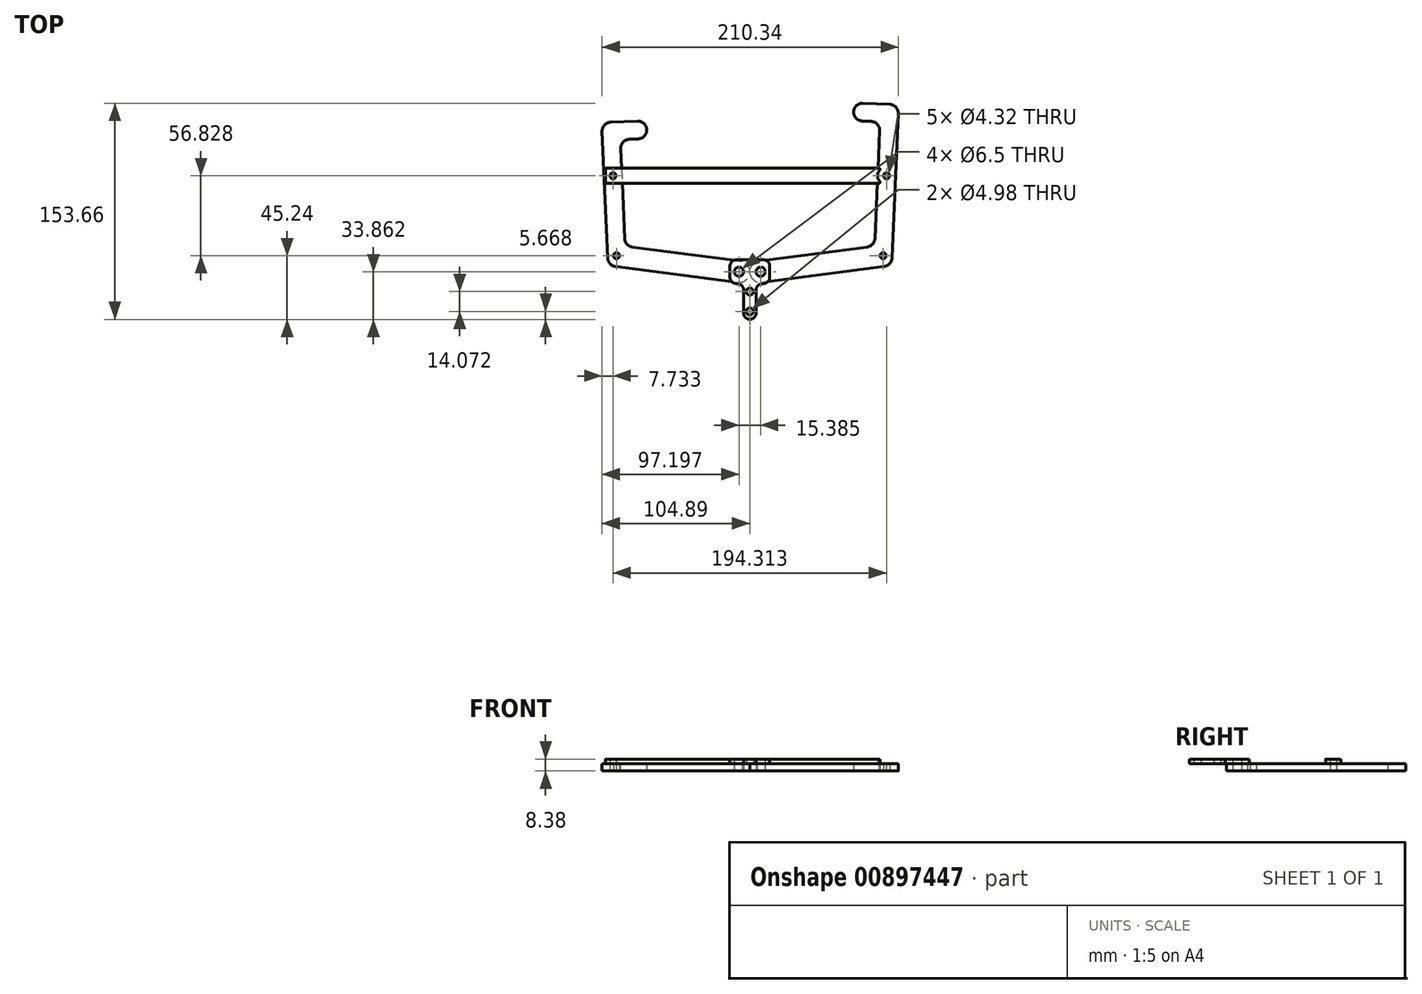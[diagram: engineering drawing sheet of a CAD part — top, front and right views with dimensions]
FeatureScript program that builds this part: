
annotation { "Feature Type Name" : "Feature", "Feature Type Description" : "" }
export const myFeature = defineFeature(function(context is Context, id is Id, definition is map)
    precondition{}
    {
        {
            var Q0;
            Q0=qCreatedBy(makeId("Top.planeOp"),FACE);
            var sketch = newSketch(context, id + "F0", { "sketchPlane" : qUnion([Q0])});
            skLineSegment(sketch, "E0", {"start": v(-105.16, 38.56) * mm, "end": v(-73.44, 39.95) * mm});
            skLineSegment(sketch, "E1", {"start": v(-105.16, 38.56) * mm, "end": v(-100.73, -62.94) * mm});
            skLineSegment(sketch, "E2", {"start": v(-100.73, -62.94) * mm, "end": v(-8.7, -75.06) * mm});
            skCircle(sketch, "E3", {"center": v(-94.68, -56.05) * mm, "radius": 2.16 * mm});
            skCircle(sketch, "E4.MirrorC", {"center": v(94.68, -56.05) * mm, "radius": 2.16 * mm});
            skLineSegment(sketch, "E5", {"start": v(-73.44, 39.95) * mm, "end": v(-72.89, 27.26) * mm});
            skLineSegment(sketch, "E6", {"start": v(-72.89, 27.26) * mm, "end": v(-91.92, 26.43) * mm});
            skLineSegment(sketch, "E7", {"start": v(-91.92, 26.43) * mm, "end": v(-88.62, -49.16) * mm});
            skLineSegment(sketch, "E8", {"start": v(-88.62, -49.16) * mm, "end": v(-5.23, -60.14) * mm});
            skLineSegment(sketch, "E9.MirrorCS", {"start": v(92.47, 39.12) * mm, "end": v(88.62, -49.16) * mm});
            skLineSegment(sketch, "E10.MirrorCS", {"start": v(105.72, 51.25) * mm, "end": v(74, 52.64) * mm});
            skLineSegment(sketch, "E11.MirrorCS", {"start": v(74, 52.64) * mm, "end": v(73.44, 39.95) * mm});
            skLineSegment(sketch, "E12.MirrorCS", {"start": v(100.73, -62.94) * mm, "end": v(8.7, -75.06) * mm});
            skLineSegment(sketch, "E13.MirrorCS", {"start": v(105.72, 51.25) * mm, "end": v(100.73, -62.94) * mm});
            skLineSegment(sketch, "E14.MirrorCS", {"start": v(88.62, -49.16) * mm, "end": v(5.23, -60.14) * mm});
            skLineSegment(sketch, "E15.MirrorCS", {"start": v(73.44, 39.95) * mm, "end": v(92.47, 39.12) * mm});
            skArc(sketch, "E16", {"start": v(-8.7, -75.06) * mm, "mid": v(-0.2, -69.17) * mm, "end": v(-5.23, -60.14) * mm});
            skArc(sketch, "E17.MirrorCS", {"start": v(8.7, -75.06) * mm, "mid": v(0.2, -69.17) * mm, "end": v(5.23, -60.14) * mm});
            skPoint(sketch, "E18.orphan", {"position": v(0, -60.83) * mm});
            skPoint(sketch, "E19.orphan", {"position": v(0, -76.2) * mm});
            skLineSegment(sketch, "E20", {"start": v(-100.73, -62.94) * mm, "end": v(0, -76.2) * mm, "construction": true});
            skPoint(sketch, "E21.middle", {"position": v(0, -67.43) * mm});
            skCircle(sketch, "E22", {"center": v(-7.7, -67.43) * mm, "radius": 3.25 * mm});
            skCircle(sketch, "E23", {"center": v(7.7, -67.43) * mm, "radius": 3.25 * mm});
            skLineSegment(sketch, "E24", {"start": v(-88.62, -49.16) * mm, "end": v(-100.73, -62.94) * mm, "construction": true});
            skCircle(sketch, "E25", {"center": v(-97.16, 0.78) * mm, "radius": 2.16 * mm});
            skCircle(sketch, "E26.MirrorC", {"center": v(97.16, 0.78) * mm, "radius": 2.16 * mm});
            skLineSegment(sketch, "E27", {"start": v(-103.5, 0.5) * mm, "end": v(-90.81, 1.05) * mm, "construction": true});
            skLineSegment(sketch, "E28", {"start": v(0, -76.2) * mm, "end": v(-48.84, -76.2) * mm, "construction": true});
            skSolve(sketch);
        }
        {
            var Q0;
            Q0 = qSketchRegion(id + "F0", true);
            extrude(context, id + "F1", {"entities" : qUnion([Q0]), "depth" : 5.2 * mm, "offsetDistance" : 25.4 * mm});
        }
        {
            var Q0;
            Q0=makeQuery(id+"F1.opExtrude","CAP_FACE",FACE,{"disambiguationData":[OSD([sQuery(id+"F0.wireOp",EDGE,"E0"),sQuery(id+"F0.wireOp",EDGE,"E1"),sQuery(id+"F0.wireOp",EDGE,"E2"),sQuery(id+"F0.wireOp",EDGE,"E3"),sQuery(id+"F0.wireOp",EDGE,"E5"),sQuery(id+"F0.wireOp",EDGE,"E6"),sQuery(id+"F0.wireOp",EDGE,"E7"),sQuery(id+"F0.wireOp",EDGE,"E8"),sQuery(id+"F0.wireOp",EDGE,"E16"),sQuery(id+"F0.wireOp",EDGE,"E22"),sQuery(id+"F0.wireOp",EDGE,"E25")])],"isStart":false});
            var sketch = newSketch(context, id + "F2", { "sketchPlane" : qUnion([Q0])});
            skLineSegment(sketch, "E29.bottom", {"start": v(-4.44, -75.89) * mm, "end": v(4.45, -75.89) * mm});
            skLineSegment(sketch, "E29.top", {"start": v(-4.44, -101.29) * mm, "end": v(4.45, -101.29) * mm});
            skLineSegment(sketch, "E29.left", {"start": v(-4.44, -75.89) * mm, "end": v(-4.44, -101.29) * mm});
            skLineSegment(sketch, "E29.right", {"start": v(4.45, -75.89) * mm, "end": v(4.45, -101.29) * mm});
            skPoint(sketch, "E29.middle", {"position": v(0, -88.59) * mm});
            skCircle(sketch, "E30.0", {"center": v(-7.7, -67.43) * mm, "radius": 3.25 * mm});
            skCircle(sketch, "E30.1", {"center": v(7.7, -67.43) * mm, "radius": 3.25 * mm});
            skCircle(sketch, "E31.cCircle", {"center": v(-121.49, -83.42) * mm, "radius": 6.35 * mm, "construction": true});
            skLineSegment(sketch, "E31.0", {"start": v(-125.16, -77.07) * mm, "end": v(-117.82, -77.07) * mm});
            skLineSegment(sketch, "E31.1", {"start": v(-117.82, -77.07) * mm, "end": v(-114.16, -83.42) * mm});
            skLineSegment(sketch, "E31.2", {"start": v(-114.16, -83.42) * mm, "end": v(-117.82, -89.77) * mm});
            skLineSegment(sketch, "E31.3", {"start": v(-117.82, -89.77) * mm, "end": v(-125.16, -89.77) * mm});
            skLineSegment(sketch, "E31.4", {"start": v(-125.16, -89.77) * mm, "end": v(-128.82, -83.42) * mm});
            skLineSegment(sketch, "E31.5", {"start": v(-128.82, -83.42) * mm, "end": v(-125.16, -77.07) * mm});
            skPoint(sketch, "E31.0.midPoint", {"position": v(-121.49, -77.07) * mm});
            skLineSegment(sketch, "E32.bottom", {"start": v(-14.12, -58.97) * mm, "end": v(14.12, -58.97) * mm});
            skLineSegment(sketch, "E32.top", {"start": v(-14.12, -75.89) * mm, "end": v(14.12, -75.89) * mm});
            skLineSegment(sketch, "E32.left", {"start": v(-14.12, -58.97) * mm, "end": v(-14.12, -75.89) * mm});
            skLineSegment(sketch, "E32.right", {"start": v(14.12, -58.97) * mm, "end": v(14.12, -75.89) * mm});
            skPoint(sketch, "E32.middle", {"position": v(0, -67.43) * mm});
            skCircle(sketch, "E33", {"center": v(0, -81.55) * mm, "radius": 2.49 * mm});
            skLineSegment(sketch, "E34", {"start": v(0, -88.59) * mm, "end": v(-4.44, -88.59) * mm, "construction": true});
            skCircle(sketch, "E35.MirrorC", {"center": v(0, -95.62) * mm, "radius": 2.49 * mm});
            skSolve(sketch);
        }
        {
            var Q0;
            {var subQ1=sQuery(id+"F2.wireOp",EDGE,"E29.bottom");Q0=makeQuery(id+"F2.imprint","IMPRINT",FACE,{"disambiguationData":[TD([[makeQuery(id+"F2.imprint","IMPRINT",EDGE,{"derivedFrom":subQ1}),1.0]])]});}
            var Q1;
            Q1=makeQuery(id+"F2.imprint","IMPRINT",FACE,{"disambiguationData":[TD([[makeQuery(id+"F2.imprint","IMPRINT",EDGE,{"derivedFrom":sQuery(id+"F2.wireOp",EDGE,"E29.bottom")}),-1.0]])]});
            var Q2;
            Q2=makeQuery(id+"F2.imprint","IMPRINT",FACE,{"disambiguationData":[TD([[makeQuery(id+"F2.imprint","IMPRINT",EDGE,{"derivedFrom":sQuery(id+"F2.wireOp",EDGE,"E30.0")}),-1.0]])]});
            extrude(context, id + "F3", {"entities" : qUnion([Q0, Q1, Q2]), "depth" : 3.17 * mm, "offsetDistance" : 25.4 * mm});
        }
        {
            var Q0;
            Q0=makeQuery(id+"F3.opExtrude","SWEPT_EDGE",EDGE,{"disambiguationData":[OSD([sQuery(id+"F2.wireOp",EDGE,"E29.bottom"),sQuery(id+"F2.wireOp",EDGE,"E29.left"),sQuery(id+"F2.wireOp",EDGE,"E32.top")])]});
            var Q1;
            Q1=makeQuery(id+"F3.opExtrude","SWEPT_EDGE",EDGE,{"disambiguationData":[OSD([sQuery(id+"F2.wireOp",EDGE,"E32.top"),sQuery(id+"F2.wireOp",EDGE,"E32.left")])]});
            var Q2;
            Q2=makeQuery(id+"F3.opExtrude","SWEPT_EDGE",EDGE,{"disambiguationData":[OSD([sQuery(id+"F2.wireOp",EDGE,"E29.bottom"),sQuery(id+"F2.wireOp",EDGE,"E29.right"),sQuery(id+"F2.wireOp",EDGE,"E32.top")])]});
            var Q3;
            Q3=makeQuery(id+"F3.opExtrude","SWEPT_EDGE",EDGE,{"disambiguationData":[OSD([sQuery(id+"F2.wireOp",EDGE,"E32.top"),sQuery(id+"F2.wireOp",EDGE,"E32.right")])]});
            var Q4;
            Q4=makeQuery(id+"F3.opExtrude","SWEPT_EDGE",EDGE,{"disambiguationData":[OSD([sQuery(id+"F2.wireOp",EDGE,"E32.bottom"),sQuery(id+"F2.wireOp",EDGE,"E32.right")])]});
            var Q5;
            Q5=makeQuery(id+"F3.opExtrude","SWEPT_EDGE",EDGE,{"disambiguationData":[OSD([sQuery(id+"F0.wireOp",EDGE,"E8"),sQuery(id+"F2.wireOp",EDGE,"E32.bottom"),sQuery(id+"F2.wireOp",EDGE,"E32.left")])]});
            var Q6;
            Q6=makeQuery(id+"F3.opExtrude","SWEPT_EDGE",EDGE,{"disambiguationData":[OSD([sQuery(id+"F2.wireOp",EDGE,"E29.top"),sQuery(id+"F2.wireOp",EDGE,"E29.left")])]});
            var Q7;
            Q7=makeQuery(id+"F3.opExtrude","SWEPT_EDGE",EDGE,{"disambiguationData":[OSD([sQuery(id+"F2.wireOp",EDGE,"E29.top"),sQuery(id+"F2.wireOp",EDGE,"E29.right")])]});
            fillet(context, id + "F4", {"entities" : qUnion([Q0, Q1, Q2, Q3, Q4, Q5, Q6, Q7]), "radius" : 4.44 * mm, "tangentPropagation" : true, "allowEdgeOverflow" : false});
        }
        {
            var Q0;
            Q0=makeQuery(id+"F1.opExtrude","CAP_FACE",FACE,{"disambiguationData":[OSD([sQuery(id+"F0.wireOp",EDGE,"E9.MirrorCS"),sQuery(id+"F0.wireOp",EDGE,"E10.MirrorCS"),sQuery(id+"F0.wireOp",EDGE,"E11.MirrorCS"),sQuery(id+"F0.wireOp",EDGE,"E12.MirrorCS"),sQuery(id+"F0.wireOp",EDGE,"E13.MirrorCS"),sQuery(id+"F0.wireOp",EDGE,"E14.MirrorCS"),sQuery(id+"F0.wireOp",EDGE,"E15.MirrorCS"),sQuery(id+"F0.wireOp",EDGE,"E4.MirrorC"),sQuery(id+"F0.wireOp",EDGE,"E17.MirrorCS"),sQuery(id+"F0.wireOp",EDGE,"E23"),sQuery(id+"F0.wireOp",EDGE,"E26.MirrorC")])],"isStart":false});
            var sketch = newSketch(context, id + "F5", { "sketchPlane" : qUnion([Q0])});
            skCircle(sketch, "E36", {"center": v(97.16, 0.78) * mm, "radius": 6.35 * mm});
            skLineSegment(sketch, "E37.bottom", {"start": v(-102.5, 6.11) * mm, "end": v(93.71, 6.11) * mm});
            skLineSegment(sketch, "E37.top", {"start": v(-102.5, -4.56) * mm, "end": v(93.71, -4.56) * mm});
            skLineSegment(sketch, "E37.left", {"start": v(-102.5, 6.11) * mm, "end": v(-102.5, -4.56) * mm});
            skLineSegment(sketch, "E37.right", {"start": v(93.71, 0.78) * mm, "end": v(93.71, -4.56) * mm});
            skPoint(sketch, "E38", {"position": v(93.71, 0.78) * mm});
            skCircle(sketch, "E39.0", {"center": v(-97.16, 0.78) * mm, "radius": 2.16 * mm});
            skSolve(sketch);
        }
        {
            var Q0;
            {var subQ0=sQuery(id+"F5.wireOp",EDGE,"E37.left");Q0=makeQuery(id+"F5.imprint","IMPRINT",FACE,{"disambiguationData":[TD([[makeQuery(id+"F5.imprint","IMPRINT",EDGE,{"derivedFrom":subQ0}),1.0]])]});}
            var Q1;
            {var subQ0=sQuery(id+"F5.wireOp",EDGE,"E37.top");var subQ1=sQuery(id+"F5.wireOp",EDGE,"E36");var subQ2=makeQuery(id+"F5.imprint","INTERSECT",VERTEX,{"derivedFrom":[subQ1,subQ0]});Q1=makeQuery(id+"F5.imprint","IMPRINT",FACE,{"disambiguationData":[TD([[makeQuery(id+"F5.imprint","IMPRINT",EDGE,{"disambiguationData":[TD([[subQ2,1.0]])],"derivedFrom":subQ1}),-1.0]])]});}
            var Q2;
            {var subQ0=sQuery(id+"F5.wireOp",EDGE,"E37.bottom");var subQ1=sQuery(id+"F5.wireOp",EDGE,"E36");var subQ2=makeQuery(id+"F5.imprint","INTERSECT",VERTEX,{"derivedFrom":[subQ1,subQ0]});Q2=makeQuery(id+"F5.imprint","IMPRINT",FACE,{"disambiguationData":[TD([[makeQuery(id+"F5.imprint","IMPRINT",EDGE,{"disambiguationData":[TD([[subQ2,-1.0]])],"derivedFrom":subQ1}),-1.0]])]});}
            extrude(context, id + "F6", {"entities" : qUnion([Q0, Q1, Q2]), "depth" : 3.17 * mm, "offsetDistance" : 25.4 * mm});
        }
        {
            var Q0;
            Q0=makeQuery(id+"F6.opExtrude","SWEPT_EDGE",EDGE,{"disambiguationData":[OSD([sQuery(id+"F5.wireOp",EDGE,"E37.bottom"),sQuery(id+"F5.wireOp",EDGE,"E37.left")])]});
            var Q1;
            Q1=makeQuery(id+"F6.opExtrude","SWEPT_EDGE",EDGE,{"disambiguationData":[OSD([sQuery(id+"F5.wireOp",EDGE,"E37.top"),sQuery(id+"F5.wireOp",EDGE,"E37.left")])]});
            var Q2;
            Q2=makeQuery(id+"F6.opExtrude","SWEPT_EDGE",EDGE,{"disambiguationData":[OSD([sQuery(id+"F5.wireOp",EDGE,"E36"),sQuery(id+"F5.wireOp",EDGE,"E37.bottom")])]});
            var Q3;
            Q3=makeQuery(id+"F6.opExtrude","SWEPT_EDGE",EDGE,{"disambiguationData":[OSD([sQuery(id+"F5.wireOp",EDGE,"E36"),sQuery(id+"F5.wireOp",EDGE,"E37.top")])]});
            fillet(context, id + "F7", {"entities" : qUnion([Q0, Q1, Q2, Q3]), "radius" : 0.8 * mm, "tangentPropagation" : true, "allowEdgeOverflow" : false});
        }
        {
            var Q0;
            Q0=makeQuery(id+"F1.opExtrude","SWEPT_EDGE",EDGE,{"disambiguationData":[OSD([sQuery(id+"F0.wireOp",EDGE,"E0"),sQuery(id+"F0.wireOp",EDGE,"E5")])]});
            var Q1;
            Q1=makeQuery(id+"F1.opExtrude","SWEPT_EDGE",EDGE,{"disambiguationData":[OSD([sQuery(id+"F0.wireOp",EDGE,"E5"),sQuery(id+"F0.wireOp",EDGE,"E6")])]});
            var Q2;
            Q2=makeQuery(id+"F1.opExtrude","SWEPT_EDGE",EDGE,{"disambiguationData":[OSD([sQuery(id+"F0.wireOp",EDGE,"E0"),sQuery(id+"F0.wireOp",EDGE,"E1")])]});
            var Q3;
            Q3=makeQuery(id+"F1.opExtrude","SWEPT_EDGE",EDGE,{"disambiguationData":[OSD([sQuery(id+"F0.wireOp",EDGE,"E6"),sQuery(id+"F0.wireOp",EDGE,"E7")])]});
            var Q4;
            Q4=makeQuery(id+"F1.opExtrude","SWEPT_EDGE",EDGE,{"disambiguationData":[OSD([sQuery(id+"F0.wireOp",EDGE,"E9.MirrorCS"),sQuery(id+"F0.wireOp",EDGE,"E15.MirrorCS")])]});
            var Q5;
            Q5=makeQuery(id+"F1.opExtrude","SWEPT_EDGE",EDGE,{"disambiguationData":[OSD([sQuery(id+"F0.wireOp",EDGE,"E11.MirrorCS"),sQuery(id+"F0.wireOp",EDGE,"E15.MirrorCS")])]});
            var Q6;
            Q6=makeQuery(id+"F1.opExtrude","SWEPT_EDGE",EDGE,{"disambiguationData":[OSD([sQuery(id+"F0.wireOp",EDGE,"E10.MirrorCS"),sQuery(id+"F0.wireOp",EDGE,"E11.MirrorCS")])]});
            var Q7;
            Q7=makeQuery(id+"F1.opExtrude","SWEPT_EDGE",EDGE,{"disambiguationData":[OSD([sQuery(id+"F0.wireOp",EDGE,"E10.MirrorCS"),sQuery(id+"F0.wireOp",EDGE,"E13.MirrorCS")])]});
            var Q8;
            Q8=makeQuery(id+"F1.opExtrude","SWEPT_EDGE",EDGE,{"disambiguationData":[OSD([sQuery(id+"F0.wireOp",EDGE,"E12.MirrorCS"),sQuery(id+"F0.wireOp",EDGE,"E13.MirrorCS")])]});
            var Q9;
            Q9=makeQuery(id+"F1.opExtrude","SWEPT_EDGE",EDGE,{"disambiguationData":[OSD([sQuery(id+"F0.wireOp",EDGE,"E9.MirrorCS"),sQuery(id+"F0.wireOp",EDGE,"E14.MirrorCS")])]});
            var Q10;
            Q10=makeQuery(id+"F1.opExtrude","SWEPT_EDGE",EDGE,{"disambiguationData":[OSD([sQuery(id+"F0.wireOp",EDGE,"E1"),sQuery(id+"F0.wireOp",EDGE,"E2")])]});
            var Q11;
            Q11=makeQuery(id+"F1.opExtrude","SWEPT_EDGE",EDGE,{"disambiguationData":[OSD([sQuery(id+"F0.wireOp",EDGE,"E7"),sQuery(id+"F0.wireOp",EDGE,"E8")])]});
            var Q12;
            Q12=makeQuery(id+"FJXbDtNVVAIbCnt_2.opExtrude","SWEPT_EDGE",EDGE,{"disambiguationData":[OSD([sQuery(id+"FR1ZYMotA4mIbLd_2.wireOp",EDGE,"BIHtOTEn-8jSD-smIQ-0A3z-LjJCax1yDFBo.bottom"),sQuery(id+"FR1ZYMotA4mIbLd_2.wireOp",EDGE,"BIHtOTEn-8jSD-smIQ-0A3z-LjJCax1yDFBo.right")])]});
            var Q13;
            Q13=makeQuery(id+"FJXbDtNVVAIbCnt_2.opExtrude","SWEPT_EDGE",EDGE,{"disambiguationData":[OSD([sQuery(id+"F0.wireOp",EDGE,"E14.MirrorCS"),sQuery(id+"FR1ZYMotA4mIbLd_2.wireOp",EDGE,"BIHtOTEn-8jSD-smIQ-0A3z-LjJCax1yDFBo.bottom"),sQuery(id+"FR1ZYMotA4mIbLd_2.wireOp",EDGE,"BIHtOTEn-8jSD-smIQ-0A3z-LjJCax1yDFBo.left")])]});
            var Q14;
            Q14=makeQuery(id+"F3hmXmQMQTnAs8Z_5.opExtrude","CAP_EDGE",EDGE,{"disambiguationData":[OSD([sQuery(id+"FtWcH81dhlq3opP_5.wireOp",EDGE,"Hbn4ebLv-waTN-HL9X-xSQ3-gh0CxFL8CqY1.left")])],"isStart":false});
            var Q15;
            Q15=makeQuery(id+"F3hmXmQMQTnAs8Z_5.opExtrude","CAP_EDGE",EDGE,{"disambiguationData":[OSD([sQuery(id+"FtWcH81dhlq3opP_5.wireOp",EDGE,"Hbn4ebLv-waTN-HL9X-xSQ3-gh0CxFL8CqY1.right")])],"isStart":false});
            fillet(context, id + "F8", {"entities" : qUnion([Q0, Q1, Q2, Q3, Q4, Q5, Q6, Q7, Q8, Q9, Q10, Q11, Q12, Q13, Q14, Q15]), "radius" : 6.35 * mm, "tangentPropagation" : true, "allowEdgeOverflow" : false});
        }
    });
